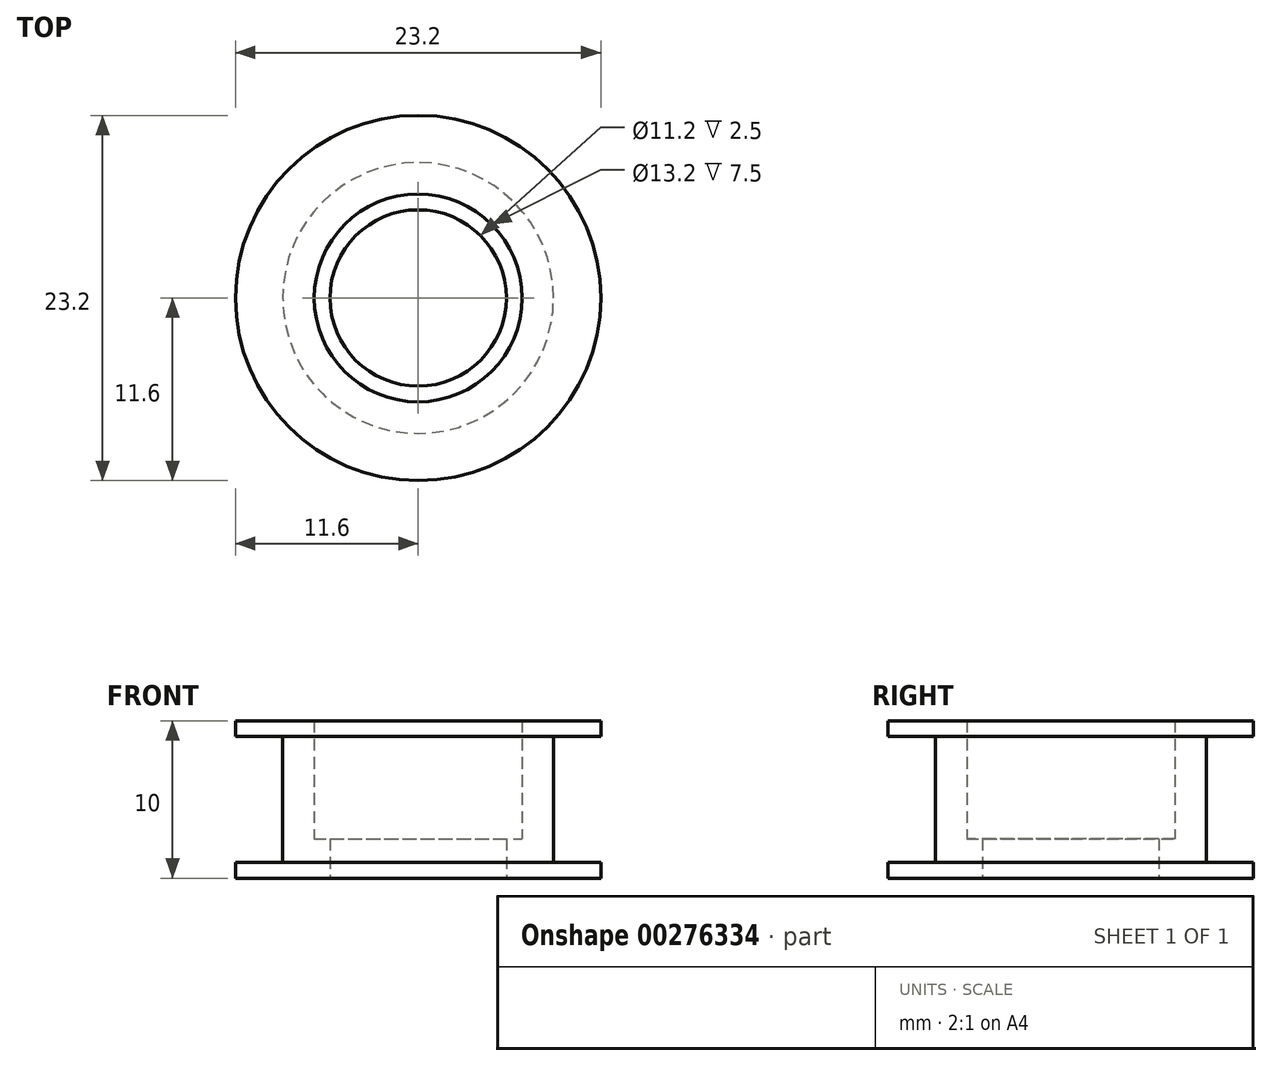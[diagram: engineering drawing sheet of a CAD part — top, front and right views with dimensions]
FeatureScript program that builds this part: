
annotation { "Feature Type Name" : "Feature", "Feature Type Description" : "" }
export const myFeature = defineFeature(function(context is Context, id is Id, definition is map)
    precondition{}
    {
        {
            var Q0;
            Q0=qCreatedBy(makeId("Top.planeOp"),FACE);
            var sketch = newSketch(context, id + "F0", { "sketchPlane" : qUnion([Q0])});
            skCircle(sketch, "E0", {"center": v(0, 0) * mm, "radius": 6.6 * mm});
            skSolve(sketch);
        }
        {
            var Q0;
            Q0=qCreatedBy(makeId("Front.planeOp"),FACE);
            var sketch = newSketch(context, id + "F1", { "sketchPlane" : qUnion([Q0])});
            skLineSegment(sketch, "E1.0", {"start": v(-6.6, 0) * mm, "end": v(6.6, 0) * mm});
            skLineSegment(sketch, "E2", {"start": v(6.6, 10) * mm, "end": v(11.6, 10) * mm});
            skLineSegment(sketch, "E3", {"start": v(11.6, 10) * mm, "end": v(11.6, 9) * mm});
            skLineSegment(sketch, "E4", {"start": v(11.6, 9) * mm, "end": v(8.6, 9) * mm});
            skLineSegment(sketch, "E5", {"start": v(8.6, 9) * mm, "end": v(8.6, 1) * mm});
            skLineSegment(sketch, "E6", {"start": v(8.6, 1) * mm, "end": v(11.6, 1) * mm});
            skLineSegment(sketch, "E7", {"start": v(11.6, 1) * mm, "end": v(11.6, 0) * mm});
            skLineSegment(sketch, "E8", {"start": v(11.6, 0) * mm, "end": v(6.6, 0) * mm});
            skLineSegment(sketch, "E9", {"start": v(0, 0) * mm, "end": v(0, 0.82) * mm, "construction": true});
            skLineSegment(sketch, "E10", {"start": v(5.6, 2.5) * mm, "end": v(5.6, 0) * mm});
            skLineSegment(sketch, "E11", {"start": v(5.6, 0) * mm, "end": v(6.6, 0) * mm});
            skLineSegment(sketch, "E12", {"start": v(6.6, 10) * mm, "end": v(6.6, 2.5) * mm});
            skLineSegment(sketch, "E13", {"start": v(6.6, 2.5) * mm, "end": v(5.6, 2.5) * mm});
            skSolve(sketch);
        }
        {
            var Q0;
            Q0=makeQuery(id+"F1.imprint","IMPRINT",FACE,{"disambiguationData":[TD([[makeQuery(id+"F1.imprint","IMPRINT",EDGE,{"derivedFrom":sQuery(id+"F1.wireOp",EDGE,"E2")}),-1.0]])]});
            var Q1;
            Q1=sQuery(id+"F1.wireOp",EDGE,"E9");
            revolve(context, id + "F2", {"entities" : qUnion([Q0]), "axis" : qUnion([Q1]), "revolveType" : RevolveType.FULL});
        }
    });
